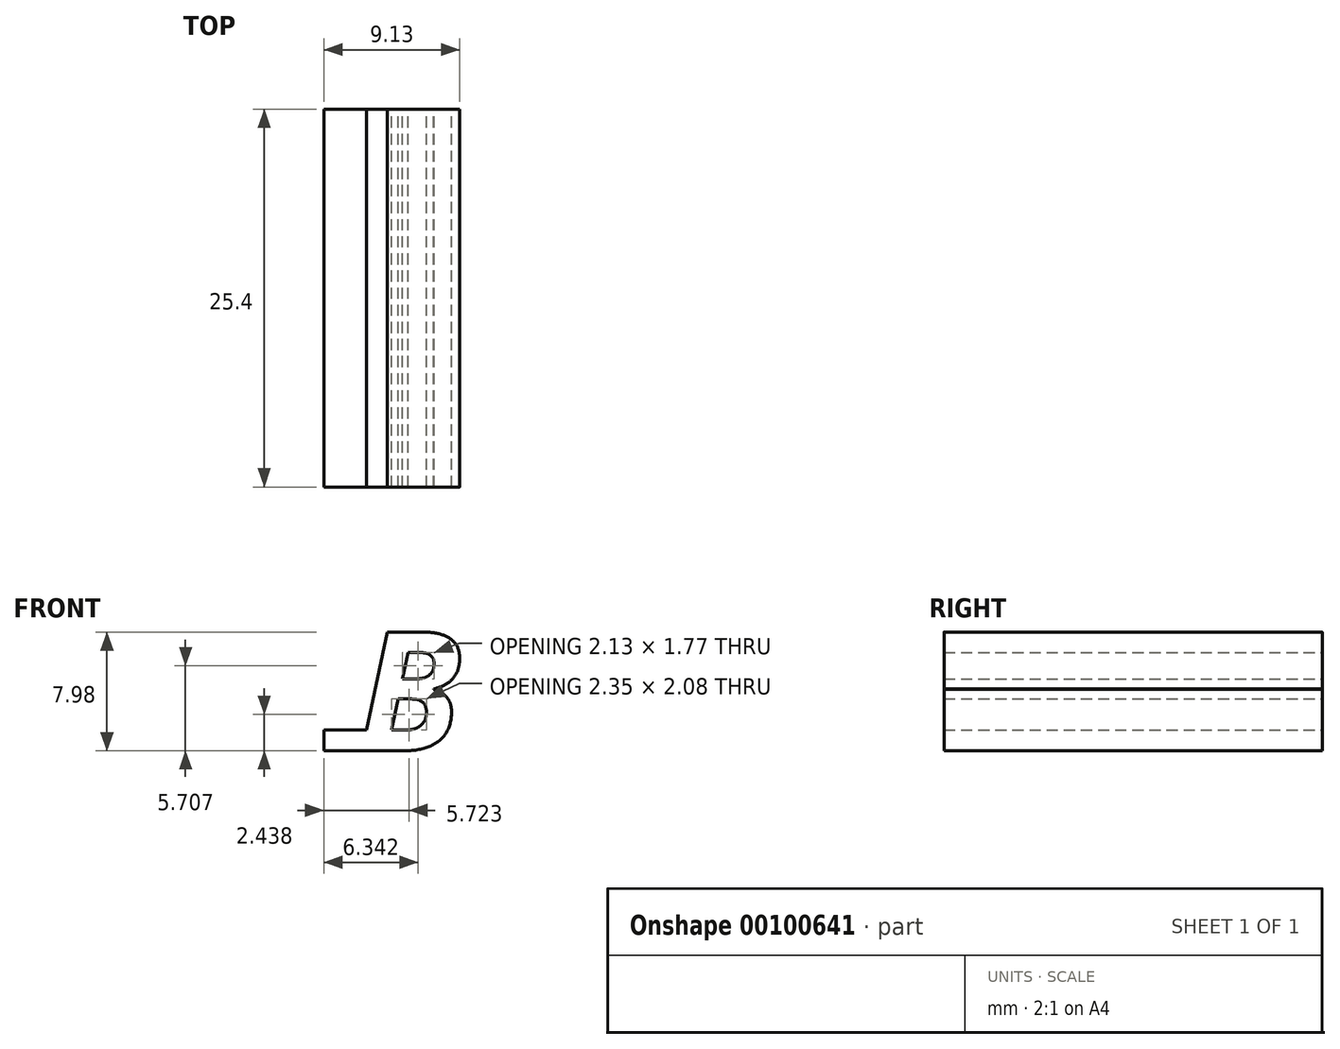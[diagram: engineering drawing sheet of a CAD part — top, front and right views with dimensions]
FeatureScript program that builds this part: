
annotation { "Feature Type Name" : "Feature", "Feature Type Description" : "" }
export const myFeature = defineFeature(function(context is Context, id is Id, definition is map)
    precondition{}
    {
        {
            var Q0;
            Q0=qCreatedBy(makeId("Front.planeOp"),FACE);
            var sketch = newSketch(context, id + "F0", { "sketchPlane" : qUnion([Q0])});
            skText(sketch, "E0", { "text": "NB\n", "fontName": "NotoSans-BoldItalic.ttf"});
            skLineSegment(sketch, "E1.bottom", {"start": v(-9.5, 0.05) * mm, "end": v(-6.33, 0.05) * mm});
            skLineSegment(sketch, "E2.bottom", {"start": v(-5.3, 1.44) * mm, "end": v(-9.86, 1.44) * mm});
            skLineSegment(sketch, "E2.top", {"start": v(-5.3, 0.05) * mm, "end": v(-9.86, 0.05) * mm});
            skLineSegment(sketch, "E2.left", {"start": v(-5.3, 1.44) * mm, "end": v(-5.3, 0.05) * mm});
            skLineSegment(sketch, "E2.right", {"start": v(-9.86, 1.44) * mm, "end": v(-9.86, 0.05) * mm});
            const initialGuessF0  = {"E0": [-0.016, 5e-05, 1, 0, 0.00805]};
            skSetInitialGuess(sketch, initialGuessF0);
            skSolve(sketch);
        }
        {
            var Q0;
            Q0=makeQuery(id+"F0.imprint","IMPRINT",FACE,{"disambiguationData":[TD([[makeQuery(id+"F0.imprint","IMPRINT",EDGE,{"derivedFrom":sQuery(id+"F0.wireOp",EDGE,"E0.sketch_text.stroke-0")}),-1.0]])]});
            var Q1;
            {var subQ5=sQuery(id+"F0.wireOp",EDGE,"E2.right");Q1=makeQuery(id+"F0.imprint","IMPRINT",FACE,{"disambiguationData":[TD([[makeQuery(id+"F0.imprint","IMPRINT",EDGE,{"derivedFrom":subQ5}),1.0]])]});}
            var Q2;
            {var subQ0=sQuery(id+"F0.wireOp",EDGE,"E2.top");var subQ1=sQuery(id+"F0.wireOp",EDGE,"E0.sketch_text.stroke-14");var subQ2=makeQuery(id+"F0.imprint","INTERSECT",VERTEX,{"derivedFrom":[subQ1,subQ0]});Q2=makeQuery(id+"F0.imprint","IMPRINT",FACE,{"disambiguationData":[TD([[makeQuery(id+"F0.imprint","IMPRINT",EDGE,{"disambiguationData":[TD([[subQ2,1.0]])],"derivedFrom":subQ1}),1.0]])]});}
            var Q3;
            {var subQ5=sQuery(id+"F0.wireOp",EDGE,"E2.left");Q3=makeQuery(id+"F0.imprint","IMPRINT",FACE,{"disambiguationData":[TD([[makeQuery(id+"F0.imprint","IMPRINT",EDGE,{"derivedFrom":subQ5}),-1.0]])]});}
            var Q4;
            Q4=makeQuery(id+"F0.imprint","IMPRINT",FACE,{"disambiguationData":[TD([[makeQuery(id+"F0.imprint","IMPRINT",EDGE,{"derivedFrom":sQuery(id+"F0.wireOp",EDGE,"E0.sketch_text.stroke-15")}),-1.0]])]});
            extrude(context, id + "F1", {"entities" : qUnion([Q0, Q1, Q2, Q3, Q4]), "depth" : 25.4 * mm});
        }
    });
